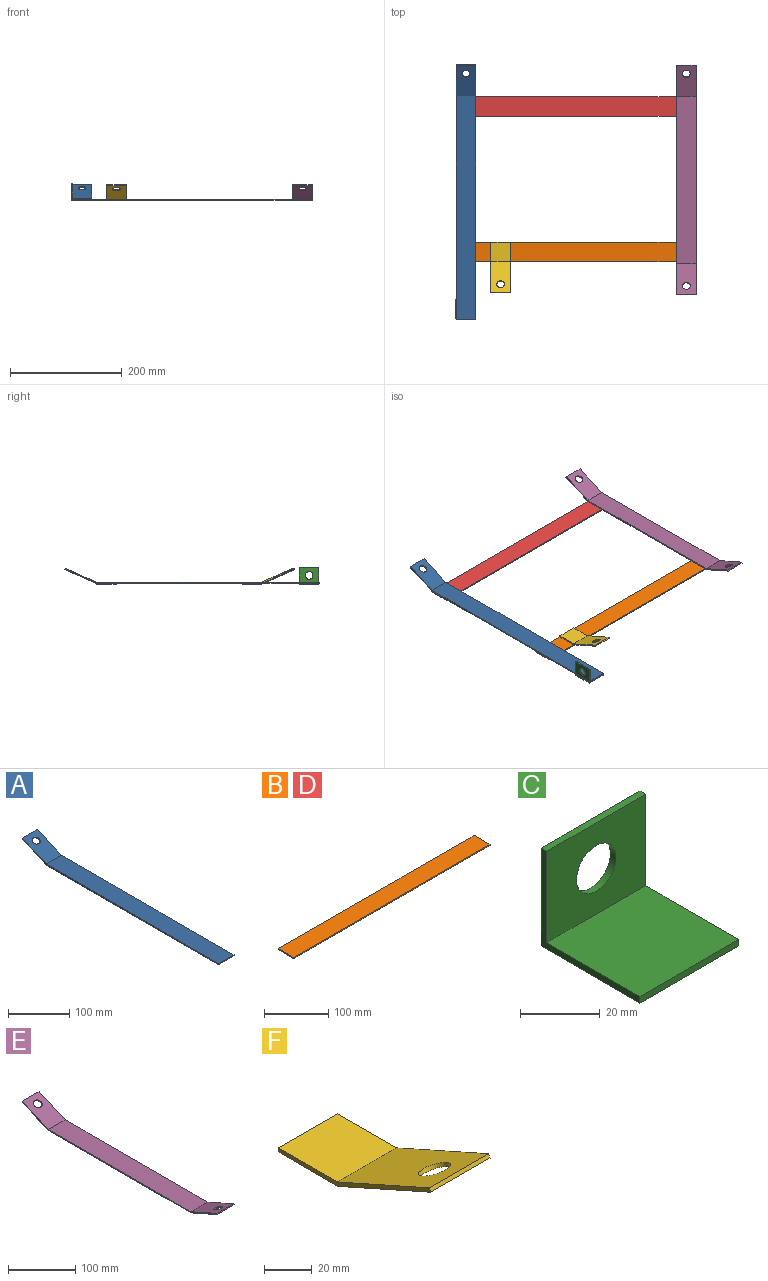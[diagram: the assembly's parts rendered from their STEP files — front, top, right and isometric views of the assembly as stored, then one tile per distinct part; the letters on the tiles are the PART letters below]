
ASSEMBLY  parts=6 mates=9
PART A: 9 faces, bbox 35x455.6x26.4 mm
  f0: plane 35x2mm, normal (0,-1,0), area 70mm2, adj f1,f3,f5,f7
  f1: plane 455.63x26.4mm, normal (-1,0,0), area 920.9mm2, adj f0,f2,f4,f5,f6,f7
  f2: plane 35x1.83mm, normal (0,0.91,0.41), area 70mm2, adj f1,f3,f4,f6
  f3: plane 455.63x26.4mm, normal (1,0,0), area 920.9mm2, adj f0,f2,f4,f5,f6,f7
  f4: plane 55.2x35mm, normal (0,0.41,-0.91), area 1960.9mm2, adj f1,f2,f3,f5,f8
  f5: plane 400.43x35mm, normal (0,0,-1), area 14014.9mm2, adj f0,f1,f3,f4
  f6: plane 54.81x35mm, normal (0,-0.41,0.91), area 1946.1mm2, adj f1,f2,f3,f7,f8
  f7: plane 400x35mm, normal (0,0,1), area 14000mm2, adj f0,f1,f3,f6
  f8: cylinder r=7mm len=14mm, axis (0,0.41,-0.91), area 88mm2, adj f4,f6
PART B: 6 faces, bbox 430x35x2 mm
  f0: plane 35x2mm, normal (-1,0,0), area 70mm2, adj f1,f3,f4,f5
  f1: plane 430x2mm, normal (0,-1,0), area 860mm2, adj f0,f2,f4,f5
  f2: plane 35x2mm, normal (1,0,0), area 70mm2, adj f1,f3,f4,f5
  f3: plane 430x2mm, normal (0,1,0), area 860mm2, adj f0,f2,f4,f5
  f4: plane 430x35mm, normal (0,0,1), area 15050mm2, adj f0,f1,f2,f3
  f5: plane 430x35mm, normal (0,0,-1), area 15050mm2, adj f0,f1,f2,f3
PART C: 9 faces, bbox 35x35x30 mm
  f0: plane 35x2mm, normal (0,-1,0), area 70mm2, adj f1,f3,f5,f7
  f1: plane 35x30mm, normal (-1,0,0), area 126mm2, adj f0,f2,f4,f5,f6,f7
  f2: plane 35x2mm, normal (0,0,1), area 70mm2, adj f1,f3,f4,f6
  f3: plane 35x30mm, normal (1,0,0), area 126mm2, adj f0,f2,f4,f5,f6,f7
  f4: plane 35x30mm, normal (0,1,0), area 896.1mm2, adj f1,f2,f3,f5,f8
  f5: plane 35x35mm, normal (0,0,-1), area 1225mm2, adj f0,f1,f3,f4
  f6: plane 35x28mm, normal (0,-1,0), area 826.1mm2, adj f1,f2,f3,f7,f8
  f7: plane 35x33mm, normal (0,0,1), area 1155mm2, adj f0,f1,f3,f6
  f8: cylinder r=7mm len=14mm, axis (0,-1,0), area 88mm2, adj f4,f6
PART D: same geometry as B
PART E: 12 faces, bbox 35x411.3x26.4 mm
  f0: plane 35x1.83mm, normal (0,-0.91,0.41), area 70mm2, adj f1,f3,f5,f8
  f1: plane 411.25x26.4mm, normal (-1,0,0), area 841.7mm2, adj f0,f2,f4,f5,f6,f7,f8,f9
  f2: plane 35x1.83mm, normal (0,0.91,0.41), area 70mm2, adj f1,f3,f4,f7
  f3: plane 411.25x26.4mm, normal (1,0,0), area 841.7mm2, adj f0,f2,f4,f5,f6,f7,f8,f9
  f4: plane 55.2x35mm, normal (0,0.41,-0.91), area 1960.9mm2, adj f1,f2,f3,f6,f10
  f5: plane 55.2x35mm, normal (0,-0.41,-0.91), area 1960.9mm2, adj f0,f1,f3,f6,f11
  f6: plane 300.85x35mm, normal (0,0,-1), area 10529.8mm2, adj f1,f3,f4,f5
  f7: plane 54.81x35mm, normal (0,-0.41,0.91), area 1946.1mm2, adj f1,f2,f3,f9,f10
  f8: plane 54.81x35mm, normal (0,0.41,0.91), area 1946.1mm2, adj f0,f1,f3,f9,f11
  f9: plane 300x35mm, normal (0,0,1), area 10500mm2, adj f1,f3,f7,f8
  f10: cylinder r=7mm len=14mm, axis (0,0.41,-0.91), area 88mm2, adj f4,f7
  f11: cylinder r=7mm len=14mm, axis (0,-0.41,-0.91), area 88mm2, adj f5,f8
PART F: 9 faces, bbox 35x90.6x26.4 mm
  f0: plane 90.63x26.4mm, normal (-1,0,0), area 190.9mm2, adj f1,f3,f4,f5,f6,f7
  f1: plane 35x2mm, normal (0,1,0), area 70mm2, adj f0,f2,f5,f7
  f2: plane 90.63x26.4mm, normal (1,0,0), area 190.9mm2, adj f1,f3,f4,f5,f6,f7
  f3: plane 35x1.83mm, normal (0,-0.91,0.41), area 70mm2, adj f0,f2,f4,f6
  f4: plane 55.2x35mm, normal (0,-0.41,-0.91), area 1960.9mm2, adj f0,f2,f3,f5,f8
  f5: plane 35.43x35mm, normal (0,0,-1), area 1239.9mm2, adj f0,f1,f2,f4
  f6: plane 54.81x35mm, normal (0,0.41,0.91), area 1946.1mm2, adj f0,f2,f3,f7,f8
  f7: plane 35x35mm, normal (0,0,1), area 1225mm2, adj f0,f1,f2,f6
  f8: cylinder r=7mm len=14mm, axis (0,-0.41,-0.91), area 88mm2, adj f4,f6
PLACE A t=(26.48,-206.13,599.51)mm fixed
PLACE B t=(26.48,-299.38,595.51)mm
PLACE C rot(axis=(0,0,1),90deg) t=(60.75,-401.66,595.51)mm
PLACE D t=(26.48,-38.2,595.51)mm
PLACE E t=(421.48,-106.57,599.51)mm
PLACE F t=(88.41,-103.44,599.51)mm
MATE planar B.f2 <-> E.f3  axis (1,0,0) through (456.48,-281.88,596.51)mm
MATE planar A.f5 <-> C.f7  axis (0,0,-1) through (43.98,-402.07,597.51)mm
MATE planar D.f5 <-> B.f5  axis (0,0,-1) through (241.48,-20.7,595.51)mm
MATE planar B.f2 <-> D.f2  axis (1,0,0) through (456.48,-281.88,596.51)mm
MATE planar B.f4 <-> F.f5  axis (0,0,1) through (241.48,-281.88,597.51)mm
MATE planar B.f3 <-> F.f1  axis (0,1,0) through (241.48,-264.38,596.51)mm
MATE planar B.f4 <-> E.f6  axis (0,0,1) through (241.48,-281.88,597.51)mm
MATE planar B.f4 <-> A.f5  axis (0,0,1) through (241.48,-281.88,597.51)mm
MATE planar B.f0 <-> A.f1  axis (-1,0,0) through (26.48,-281.88,596.51)mm
